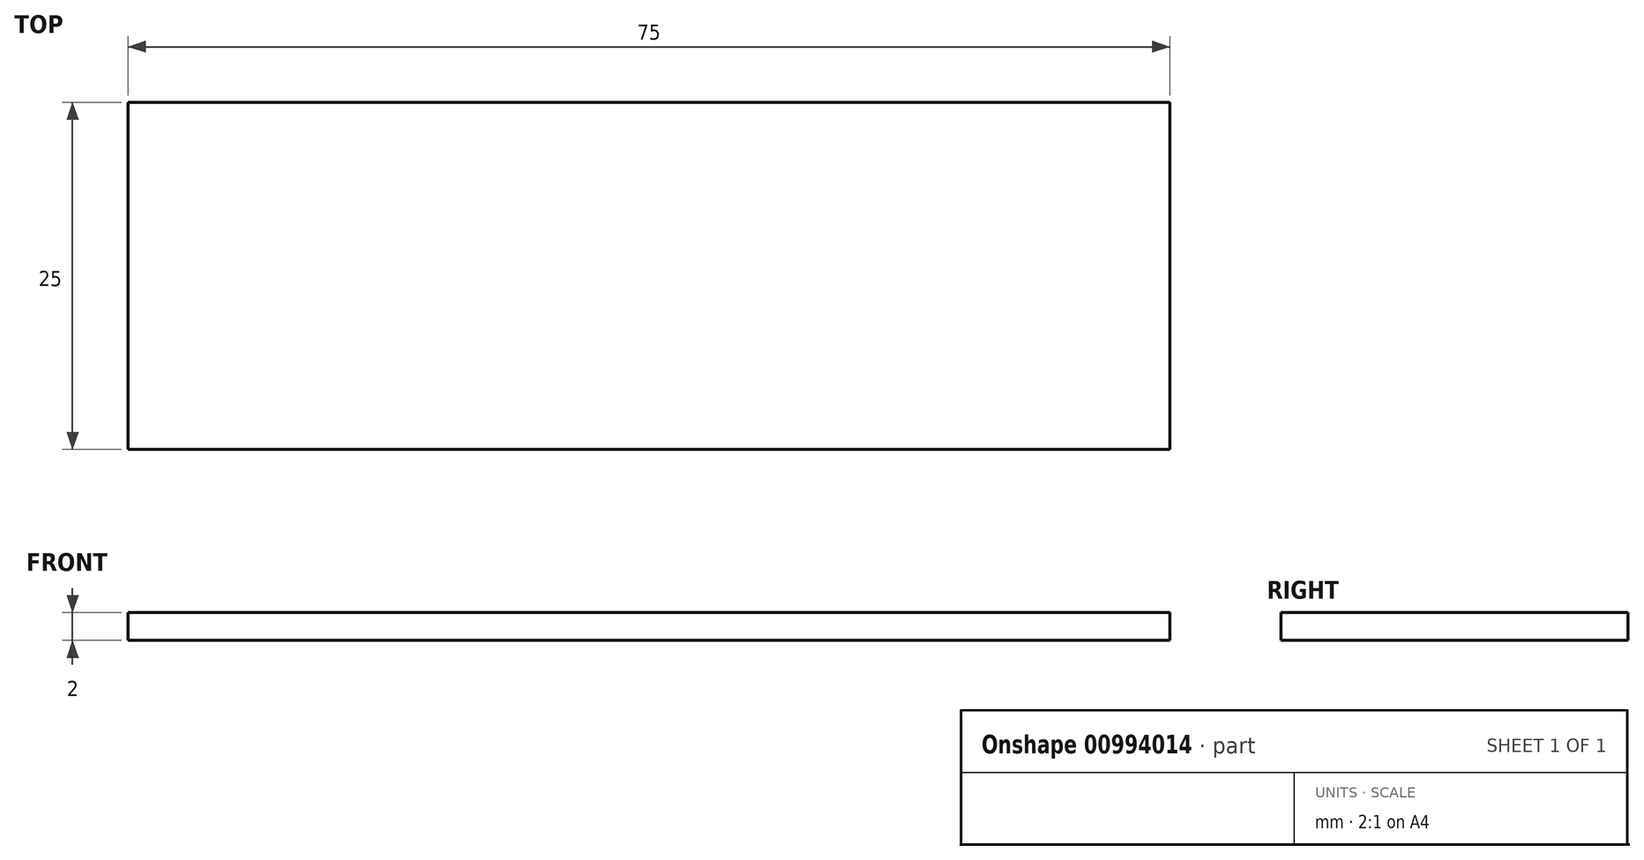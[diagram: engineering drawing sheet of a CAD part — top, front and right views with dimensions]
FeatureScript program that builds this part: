
annotation { "Feature Type Name" : "Feature", "Feature Type Description" : "" }
export const myFeature = defineFeature(function(context is Context, id is Id, definition is map)
    precondition{}
    {
        {
            var Q0;
            Q0=qCreatedBy(makeId("Top.planeOp"),FACE);
            var sketch = newSketch(context, id + "F0", { "sketchPlane" : qUnion([Q0])});
            skLineSegment(sketch, "E0.bottom", {"start": v(37.5, -12.5) * mm, "end": v(-37.5, -12.5) * mm});
            skLineSegment(sketch, "E0.top", {"start": v(37.5, 12.5) * mm, "end": v(-37.5, 12.5) * mm});
            skLineSegment(sketch, "E0.left", {"start": v(37.5, -12.5) * mm, "end": v(37.5, 12.5) * mm});
            skLineSegment(sketch, "E0.right", {"start": v(-37.5, -12.5) * mm, "end": v(-37.5, 12.5) * mm});
            skPoint(sketch, "E0.middle", {"position": v(0, 0) * mm});
            skSolve(sketch);
        }
        {
            var Q0;
            Q0 = qSketchRegion(id + "F0", true);
            var Q1;
            Q1=makeQuery(id+"F0.imprint","IMPRINT",FACE,{"disambiguationData":[TD([[makeQuery(id+"F0.imprint","IMPRINT",EDGE,{"derivedFrom":sQuery(id+"F0.wireOp",EDGE,"E0.bottom")}),-1.0]])]});
            extrude(context, id + "F1", {"entities" : qUnion([Q0, Q1]), "depth" : 2 * mm, "offsetDistance" : 25 * mm});
        }
    });
